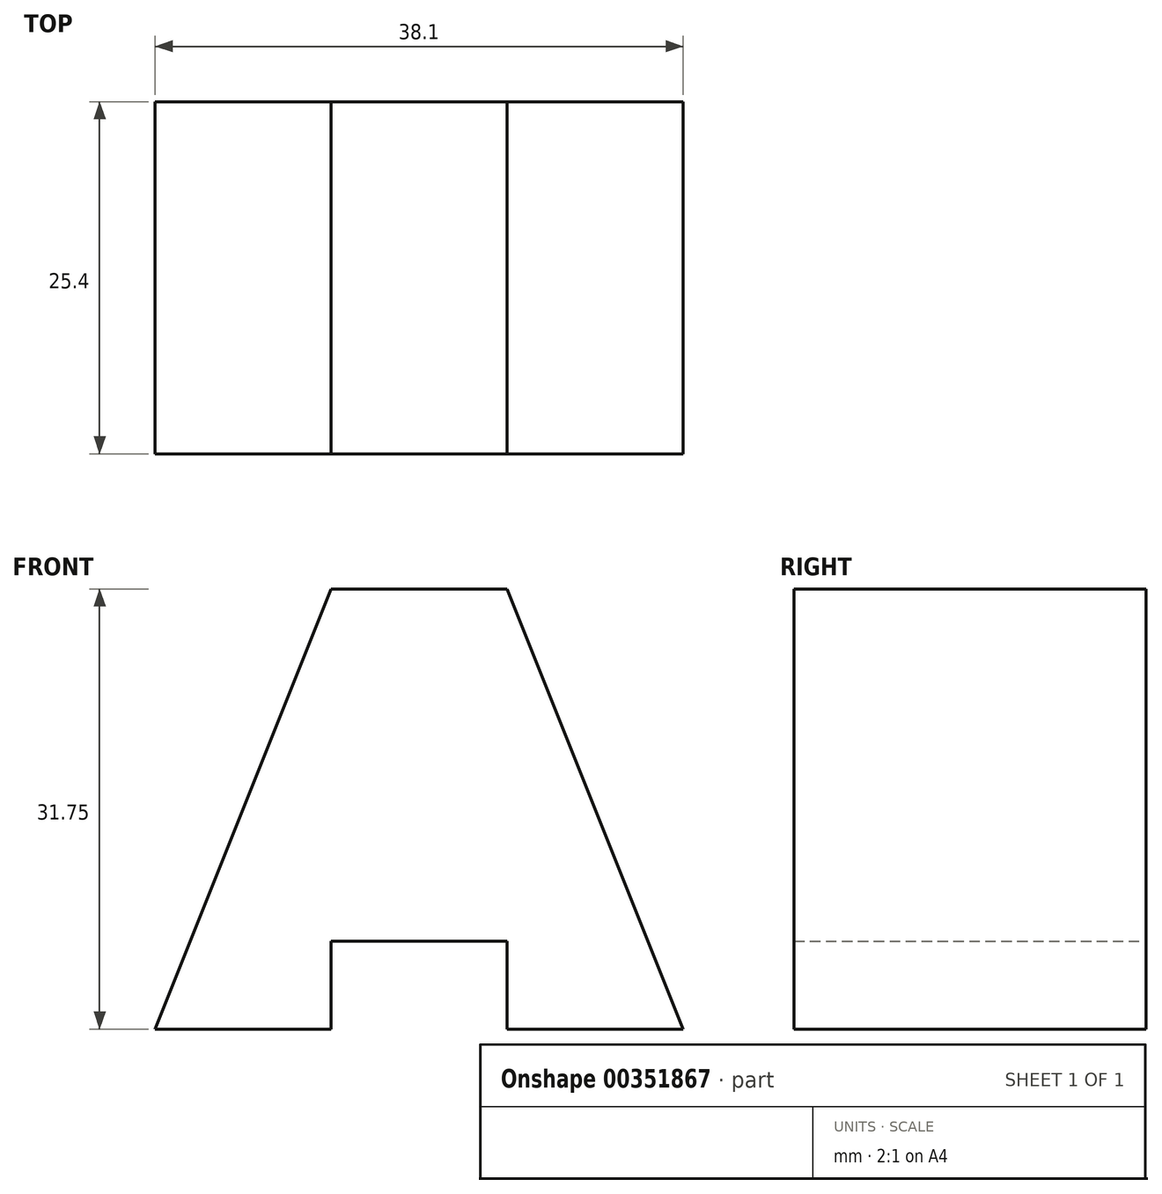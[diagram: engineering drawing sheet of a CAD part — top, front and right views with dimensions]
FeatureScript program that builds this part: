
annotation { "Feature Type Name" : "Feature", "Feature Type Description" : "" }
export const myFeature = defineFeature(function(context is Context, id is Id, definition is map)
    precondition{}
    {
        {
            var Q0;
            Q0=qCreatedBy(makeId("Front.planeOp"),FACE);
            var sketch = newSketch(context, id + "F0", { "sketchPlane" : qUnion([Q0])});
            skLineSegment(sketch, "E0", {"start": v(0, 0) * mm, "end": v(12.7, 0) * mm});
            skLineSegment(sketch, "E1", {"start": v(12.7, 0) * mm, "end": v(12.7, 6.35) * mm});
            skLineSegment(sketch, "E2", {"start": v(12.7, 6.35) * mm, "end": v(25.4, 6.35) * mm});
            skLineSegment(sketch, "E3", {"start": v(25.4, 6.35) * mm, "end": v(25.4, 0) * mm});
            skLineSegment(sketch, "E4", {"start": v(25.4, 0) * mm, "end": v(38.1, 0) * mm});
            skLineSegment(sketch, "E5", {"start": v(38.1, 0) * mm, "end": v(38.1, 31.75) * mm});
            skLineSegment(sketch, "E6", {"start": v(38.1, 31.75) * mm, "end": v(0, 31.75) * mm});
            skLineSegment(sketch, "E7", {"start": v(0, 31.75) * mm, "end": v(0, 0) * mm});
            skSolve(sketch);
        }
        {
            var Q0;
            Q0=makeQuery(id+"F0.imprint","IMPRINT",FACE,{"disambiguationData":[TD([[makeQuery(id+"F0.imprint","IMPRINT",EDGE,{"derivedFrom":sQuery(id+"F0.wireOp",EDGE,"E0")}),1.0]])]});
            extrude(context, id + "F1", {"entities" : qUnion([Q0]), "depth" : 25.4 * mm});
        }
        {
            var Q0;
            Q0=qCreatedBy(makeId("Front.planeOp"),FACE);
            var sketch = newSketch(context, id + "F2", { "sketchPlane" : qUnion([Q0])});
            skLineSegment(sketch, "E8", {"start": v(38.1, 0) * mm, "end": v(25.4, 31.75) * mm});
            skLineSegment(sketch, "E9", {"start": v(25.4, 31.75) * mm, "end": v(38.1, 31.75) * mm});
            skLineSegment(sketch, "E10", {"start": v(38.1, 31.75) * mm, "end": v(38.1, 0) * mm});
            skLineSegment(sketch, "E11", {"start": v(0, 0) * mm, "end": v(12.7, 31.75) * mm});
            skLineSegment(sketch, "E12", {"start": v(12.7, 31.75) * mm, "end": v(0, 31.75) * mm});
            skLineSegment(sketch, "E13", {"start": v(0, 31.75) * mm, "end": v(0, 0) * mm});
            skSolve(sketch);
        }
        {
            var Q0;
            Q0=makeQuery(id+"F2.imprint","IMPRINT",FACE,{"disambiguationData":[TD([[makeQuery(id+"F2.imprint","IMPRINT",EDGE,{"derivedFrom":sQuery(id+"F2.wireOp",EDGE,"E11")}),1.0]])]});
            var Q1;
            Q1=makeQuery(id+"F2.imprint","IMPRINT",FACE,{"disambiguationData":[TD([[makeQuery(id+"F2.imprint","IMPRINT",EDGE,{"derivedFrom":sQuery(id+"F2.wireOp",EDGE,"E8")}),-1.0]])]});
            extrude(context, id + "F3", {"entities" : qUnion([Q0, Q1]), "operationType" : NewBodyOperationType.REMOVE, "depth" : 25.4 * mm});
        }
    });
